# Revit family: Kabelrinne RKS- RKS 605 FS
name_source: partatom
category: Generic Models
revit_build: Autodesk Revit 2017 (Build: 20190508_0315(x64)
units: mm (PartAtom-declared; Revit-internal decimal feet)

## family parameters
Always vertical = Yes
Can host rebar = No
Cut with Voids When Loaded = No
Part Type = Normal
Room Calculation Point = No
Round Connector Dimension = Use Diameter
Shared = No
Work Plane-Based = No

## types (2) — shared parameters
Cut's number = 60
Cut's number 2 = 59
Cut's number 3 = 2
Cut's space = 50 mm  [stored 0.164042 ft]
Length = 3000 mm  [stored 9.84252 ft]
Manufacturer = OBO BETTERMANN
Material = Strip-galvanised
URL = http://www.obo-bettermann.com
Width = 1 mm  [stored 0.00328084 ft]

## per-type parameters (varying)
| type | GTIN | Manufacturer Art.No. | Width 1 | Width 2 |
| RKS 605 FS | 4012196388639 | 6055885 | 50 mm  [stored 0.164042 ft] | 25 mm  [stored 0.082021 ft] |
| RKS 607 FS | 4012196388691 | 6055893 | 70 mm  [stored 0.229659 ft] | 35 mm  [stored 0.114829 ft] |

note: column(s) folded — value = type name in every type: Article Type

note: [stored X ft] marks values corroborated as IEEE doubles in the binary element streams (Revit-internal decimal feet)

## geometry (parser evidence)
native form markers: Sweep x2
no freeform markers — native parametric forms only
